# Revit family: SystemSchroeders_2flg.Tor
name_source: partatom
category: Türen
revit_build: Autodesk Revit 2018 (Build: 20170223_1515(x64)
units: mm (PartAtom-declared; Revit-internal decimal feet)

## family parameters
Basisbauteil = Wand
Beim Laden mit Abzugskörper schneiden = Nein
Gemeinsam genutzt = Nein
Immer vertikal = Ja
OmniClass-Nummer = 23.30.10.00
OmniClass-Titel = Doors
Raumberechnungspunkt = Nein

## types (4) — shared parameters
Abstand Schlupftür = 800 mm
B02R = 4500 mm
Breite Schiebetor_R = 2200 mm
Breite Schlupftür = 1100 mm
Breite Sichtfenster = 350 mm  [stored 1.14829 ft]
Frame Projection Ext. = 25 mm  [stored 0.082021 ft]
Frame Projection Int. = 25 mm  [stored 0.082021 ft]
Frame Width = 75 mm  [stored 0.246063 ft]
Funktion = Innen
Hersteller = System Schröders
Höhe = 3000 mm  [stored 9.84252 ft]
Höhe Griff Schiebetor = 1100 mm
Höhe Griff Schlupftür = 1000 mm  [stored 3.28084 ft]
Höhe Schiebetor = 3000 mm  [stored 9.84252 ft]
T22Hang = 5 mm  [stored 0.0164042 ft]
TsileColumn = 2 mm  [stored 0.00656168 ft]
URL = https://www.system-schroeders.de
Wandabschluss = Nach Basisbauteil
Werkstoff Griff = Edelstahl
Werkstoff Rahmen = Edelstahl Rahmen
Werkstoff Schiebetor = Edelstahl Schiebetor
Werkstoff Schlupftür = Edelstahl Drehtür
Werkstoff Sichtfenster = Glas
mit Sichtfenster = Ja

## per-type parameters (varying)
| type | B02L | Breite | Breite Schiebetor_L | Einbauhöhe Sichtfenster | Feuerschutz | Höhe Schlupftür | Höhe Sichtfenster | Rauchschutz |
| ST-2 | 4600 mm | 4400 mm  [stored 14.4357 ft] | 2200 mm | 1300 mm  [stored 4.26509 ft] | EI230-Sa-C2 | 2100 mm | 450 mm  [stored 1.47638 ft] | RS |
| ST-12 | 3800 mm | 4000 mm | 1800 mm | 1500 mm  [stored 4.92126 ft] | EI290-Sa-C2 | 2000 mm | 535 mm | RS |
| RST-2 | 3800 mm | 4000 mm | 1800 mm | 1500 mm  [stored 4.92126 ft] |  | 2000 mm | 535 mm | RS |
| MST-2 | 3800 mm | 4000 mm | 1800 mm | 1500 mm  [stored 4.92126 ft] |  | 2000 mm | 535 mm |  |

note: [stored X ft] marks values corroborated as IEEE doubles in the binary element streams (Revit-internal decimal feet)

## geometry (parser evidence)
native form markers: Sweep x3
no freeform markers — native parametric forms only
